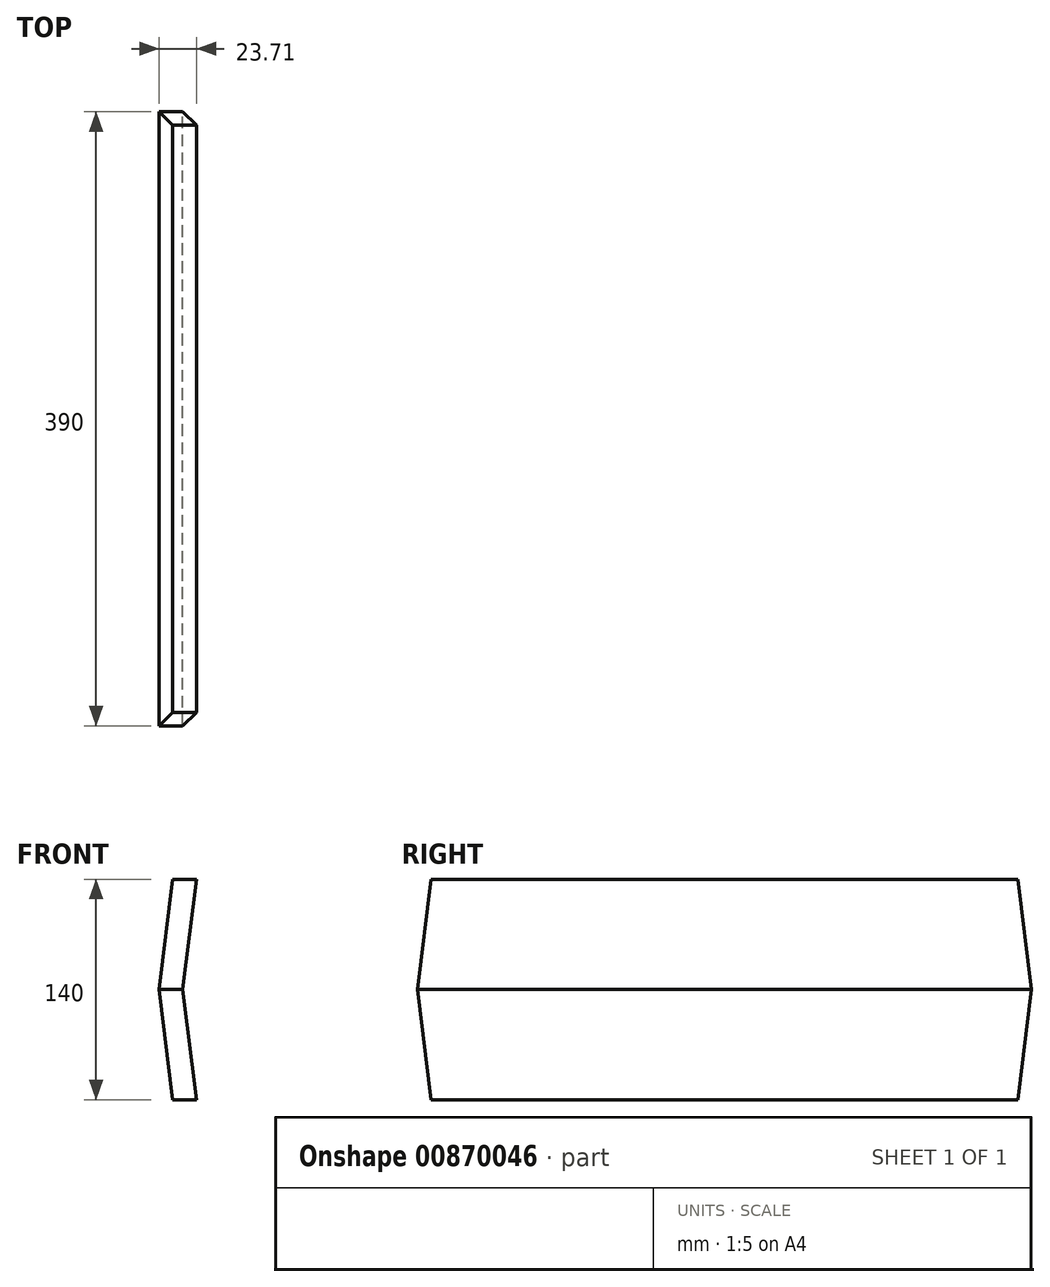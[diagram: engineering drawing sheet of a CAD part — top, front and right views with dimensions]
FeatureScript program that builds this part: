
annotation { "Feature Type Name" : "Feature", "Feature Type Description" : "" }
export const myFeature = defineFeature(function(context is Context, id is Id, definition is map)
    precondition{}
    {
        {
            var Q0;
            Q0=qCreatedBy(makeId("Front.planeOp"),FACE);
            var sketch = newSketch(context, id + "F0", { "sketchPlane" : qUnion([Q0])});
            skLineSegment(sketch, "E0", {"start": v(15.11, 0) * mm, "end": v(37.5, 182.27) * mm});
            skLineSegment(sketch, "E1", {"start": v(37.5, 182.27) * mm, "end": v(22.6, 184.1) * mm});
            skLineSegment(sketch, "E2", {"start": v(22.6, 184.1) * mm, "end": v(0, 0) * mm});
            skLineSegment(sketch, "E3", {"start": v(0, 0) * mm, "end": v(15.11, 0) * mm});
            skSolve(sketch);
        }
        {
            var Q0;
            Q0=qSketchRegion(id+"F0",true);
            extrude(context, id + "F1", {"entities" : qUnion([Q0]), "depth" : 460 * mm, "offsetDistance" : 25 * mm});
        }
        {
            var Q0;
            Q0=qCreatedBy(makeId("Right.planeOp"),FACE);
            var sketch = newSketch(context, id + "F2", { "sketchPlane" : qUnion([Q0])});
            skLineSegment(sketch, "E4", {"start": v(0, 0) * mm, "end": v(-8.6, 70) * mm});
            skLineSegment(sketch, "E5", {"start": v(-8.6, 70) * mm, "end": v(-381.4, 70) * mm});
            skLineSegment(sketch, "E6", {"start": v(-381.4, 70) * mm, "end": v(-390, 0) * mm});
            skLineSegment(sketch, "E7", {"start": v(-390, 0) * mm, "end": v(0, 0) * mm});
            skSolve(sketch);
        }
        {
            var Q0;
            Q0=makeQuery(id+"F2.imprint","IMPRINT",FACE,{"disambiguationData":[TD([[makeQuery(id+"F2.imprint","IMPRINT",EDGE,{"derivedFrom":sQuery(id+"F2.wireOp",EDGE,"E4")}),1.0]])]});
            extrude(context, id + "F3", {"entities" : qUnion([Q0]), "operationType" : NewBodyOperationType.INTERSECT, "endBound" : BoundingType.THROUGH_ALL, "depth" : 25 * mm, "offsetDistance" : 25 * mm});
        }
        {
            var Q0;
            Q0=makeQuery(id+"F1.opExtrude","SWEPT_BODY",BODY,{"disambiguationData":[OSD([sQuery(id+"F0.wireOp",EDGE,"E0"),sQuery(id+"F0.wireOp",EDGE,"E1"),sQuery(id+"F0.wireOp",EDGE,"E2"),sQuery(id+"F0.wireOp",EDGE,"E3")])]});
            var Q1;
            Q1=makeQuery(id+"F1.opExtrude","SWEPT_FACE",FACE,{"disambiguationData":[OSD([sQuery(id+"F0.wireOp",EDGE,"E3")])]});
            mirror(context, id + "F4", {"operationType" : NewBodyOperationType.ADD, "entities" : qUnion([Q0]), "mirrorPlane" : qUnion([Q1])});
        }
    });
